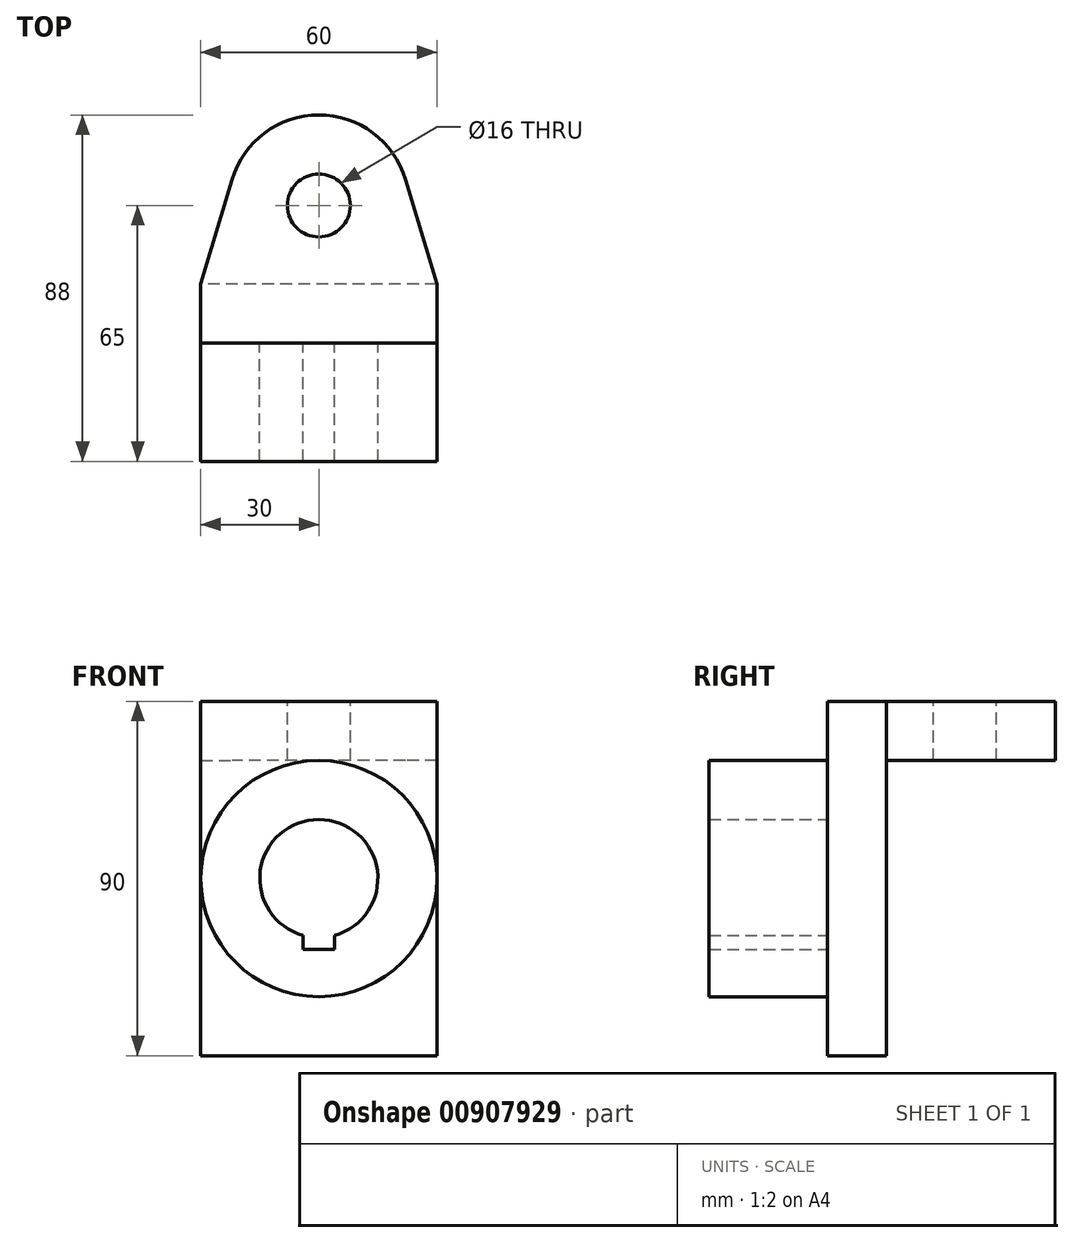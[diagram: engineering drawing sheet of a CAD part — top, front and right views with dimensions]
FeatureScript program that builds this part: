
annotation { "Feature Type Name" : "Feature", "Feature Type Description" : "" }
export const myFeature = defineFeature(function(context is Context, id is Id, definition is map)
    precondition{}
    {
        {
            var Q0;
            Q0=qCreatedBy(makeId("Front.planeOp"),FACE);
            var sketch = newSketch(context, id + "F0", { "sketchPlane" : qUnion([Q0])});
            skLineSegment(sketch, "E0.bottom", {"start": v(30, 45) * mm, "end": v(-30, 45) * mm});
            skLineSegment(sketch, "E0.top", {"start": v(30, -45) * mm, "end": v(-30, -45) * mm});
            skLineSegment(sketch, "E0.left", {"start": v(30, 45) * mm, "end": v(30, -45) * mm});
            skLineSegment(sketch, "E0.right", {"start": v(-30, 45) * mm, "end": v(-30, -45) * mm});
            skPoint(sketch, "E0.middle", {"position": v(0, 0) * mm});
            skSolve(sketch);
        }
        {
            var Q0;
            Q0 = qSketchRegion(id + "F0", true);
            extrude(context, id + "F1", {"entities" : qUnion([Q0]), "depth" : 15 * mm, "offsetDistance" : 25 * mm});
        }
        {
            var Q0;
            Q0=makeQuery(id+"F1.opExtrude","CAP_FACE",FACE,{"disambiguationData":[OSD([sQuery(id+"F0.wireOp",EDGE,"E0.bottom"),sQuery(id+"F0.wireOp",EDGE,"E0.top"),sQuery(id+"F0.wireOp",EDGE,"E0.left"),sQuery(id+"F0.wireOp",EDGE,"E0.right")])],"isStart":false});
            var sketch = newSketch(context, id + "F2", { "sketchPlane" : qUnion([Q0])});
            skCircle(sketch, "E1", {"center": v(0, 0) * mm, "radius": 30 * mm});
            skArc(sketch, "E2", {"start": v(4, -14.46) * mm, "mid": v(0, 15) * mm, "end": v(-4, -14.46) * mm});
            skLineSegment(sketch, "E3.top", {"start": v(0, -18) * mm, "end": v(4, -18) * mm});
            skLineSegment(sketch, "E3.right", {"start": v(4, -14.46) * mm, "end": v(4, -18) * mm});
            skLineSegment(sketch, "E4.MirrorCS", {"start": v(-4, -14.46) * mm, "end": v(-4, -18) * mm});
            skLineSegment(sketch, "E5.MirrorCS", {"start": v(0, -18) * mm, "end": v(-4, -18) * mm});
            skPoint(sketch, "E3.left.start.orphan", {"position": v(0, -15) * mm});
            skSolve(sketch);
        }
        {
            var Q0;
            Q0 = qSketchRegion(id + "F2", true);
            extrude(context, id + "F3", {"entities" : qUnion([Q0]), "operationType" : NewBodyOperationType.ADD, "depth" : 30 * mm, "offsetDistance" : 25 * mm});
        }
        {
            var Q0;
            Q0=makeQuery(id+"F1.opExtrude","SWEPT_FACE",FACE,{"disambiguationData":[OSD([sQuery(id+"F0.wireOp",EDGE,"E0.bottom")])]});
            var sketch = newSketch(context, id + "F4", { "sketchPlane" : qUnion([Q0])});
            skArc(sketch, "E6", {"start": v(22.03, 26.6) * mm, "mid": v(0, 43) * mm, "end": v(-22.03, 26.6) * mm});
            skCircle(sketch, "E7", {"center": v(0, 20) * mm, "radius": 8 * mm});
            skLineSegment(sketch, "E8", {"start": v(-30, 0) * mm, "end": v(30, 0) * mm});
            skLineSegment(sketch, "E9", {"start": v(30, 0) * mm, "end": v(22.03, 26.6) * mm});
            skLineSegment(sketch, "E10", {"start": v(-30, 0) * mm, "end": v(-22.03, 26.6) * mm});
            skSolve(sketch);
        }
        {
            var Q0;
            Q0 = qSketchRegion(id + "F4", true);
            extrude(context, id + "F5", {"entities" : qUnion([Q0]), "operationType" : NewBodyOperationType.ADD, "oppositeDirection" : true, "depth" : 15 * mm, "offsetDistance" : 25 * mm});
        }
    });
